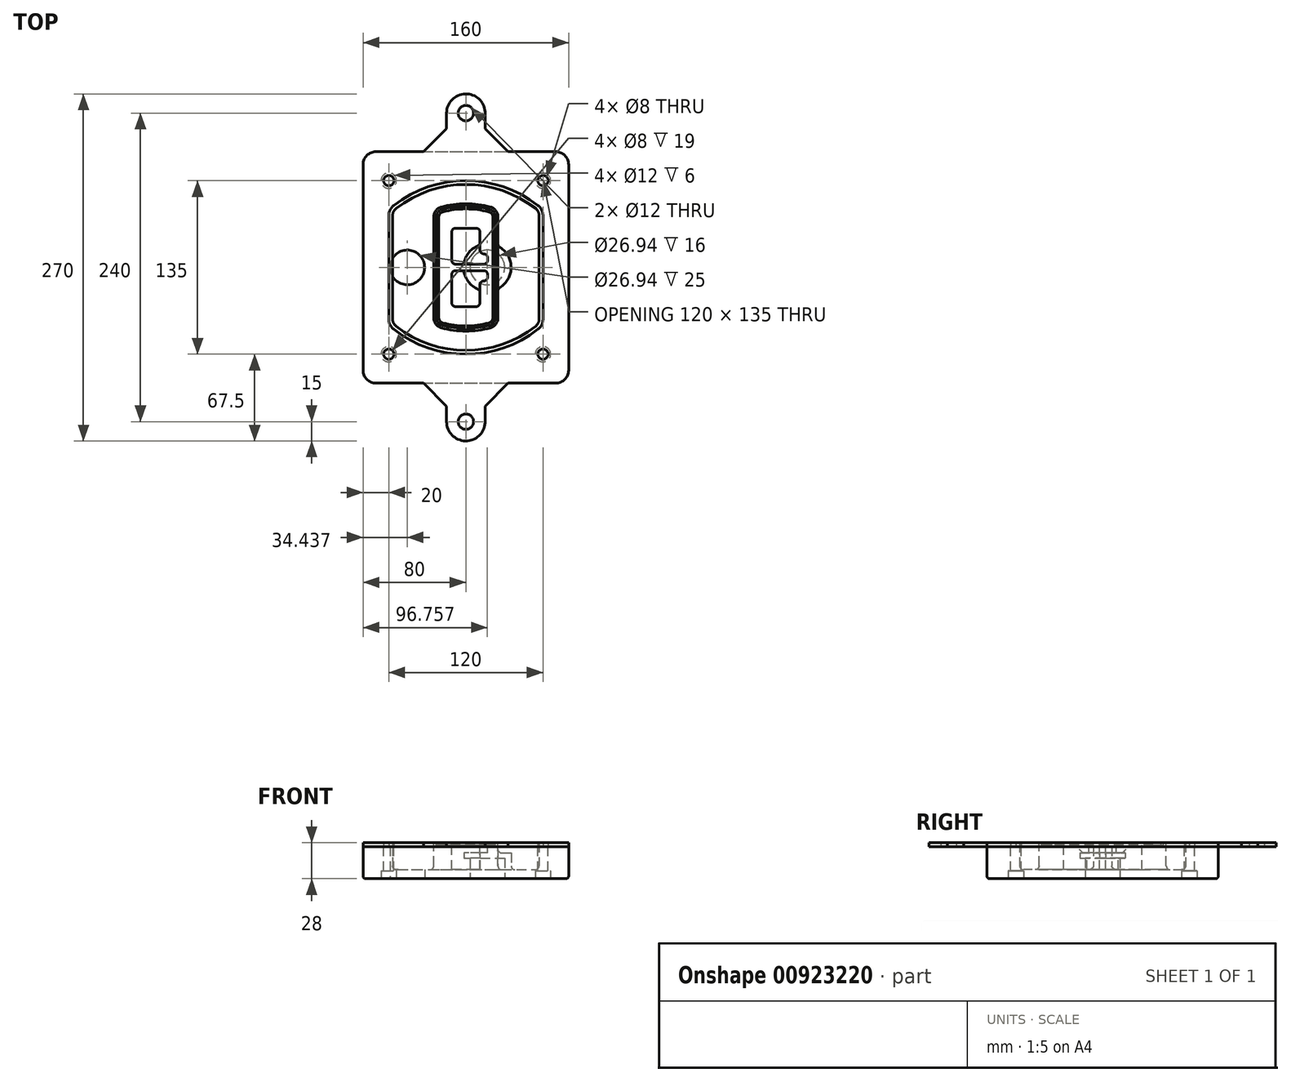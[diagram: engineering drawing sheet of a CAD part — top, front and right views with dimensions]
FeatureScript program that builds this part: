
annotation { "Feature Type Name" : "Feature", "Feature Type Description" : "" }
export const myFeature = defineFeature(function(context is Context, id is Id, definition is map)
    precondition{}
    {
        {
            var Q0;
            Q0=qCreatedBy(makeId("Top.planeOp"),FACE);
            var sketch = newSketch(context, id + "F0", { "sketchPlane" : qUnion([Q0])});
            skPoint(sketch, "E0.rect.middle", {"position": v(0, 0) * mm});
            skLineSegment(sketch, "E1.bottom", {"start": v(-70, -90) * mm, "end": v(70, -90) * mm});
            skLineSegment(sketch, "E1.top", {"start": v(-70, 90) * mm, "end": v(70, 90) * mm});
            skLineSegment(sketch, "E1.left", {"start": v(-80, -80) * mm, "end": v(-80, 80) * mm});
            skLineSegment(sketch, "E1.right", {"start": v(80, -80) * mm, "end": v(80, 80) * mm});
            skLineSegment(sketch, "E2", {"start": v(-80, 90) * mm, "end": v(80, -90) * mm, "construction": true});
            skLineSegment(sketch, "E3", {"start": v(80, 90) * mm, "end": v(-80, -90) * mm, "construction": true});
            skCircle(sketch, "E4", {"center": v(-60, 67.5) * mm, "radius": 4 * mm});
            skCircle(sketch, "E5", {"center": v(60, 67.5) * mm, "radius": 4 * mm});
            skCircle(sketch, "E6", {"center": v(60, -67.5) * mm, "radius": 4 * mm});
            skCircle(sketch, "E7", {"center": v(-60, -67.5) * mm, "radius": 4 * mm});
            skLineSegment(sketch, "E8", {"start": v(-60, 67.5) * mm, "end": v(60, 67.5) * mm, "construction": true});
            skLineSegment(sketch, "E9", {"start": v(60, 67.5) * mm, "end": v(60, -67.5) * mm, "construction": true});
            skLineSegment(sketch, "E10", {"start": v(60, -67.5) * mm, "end": v(-60, -67.5) * mm, "construction": true});
            skLineSegment(sketch, "E11", {"start": v(-60, -67.5) * mm, "end": v(-60, 67.5) * mm, "construction": true});
            skLineSegment(sketch, "E12", {"start": v(-60, 40.3) * mm, "end": v(-60, -40.3) * mm});
            skLineSegment(sketch, "E13", {"start": v(60, 40.3) * mm, "end": v(60, -40.3) * mm});
            skArc(sketch, "E14", {"start": v(56.15, 48.18) * mm, "mid": v(0, 67.5) * mm, "end": v(-56.15, 48.18) * mm});
            skArc(sketch, "E15", {"start": v(-56.15, -48.18) * mm, "mid": v(0, -67.5) * mm, "end": v(56.15, -48.18) * mm});
            skLineSegment(sketch, "E16", {"start": v(-60, 0) * mm, "end": v(60, 0) * mm, "construction": true});
            skPoint(sketch, "E17.visualSharp", {"position": v(-60, -45) * mm});
            skArc(sketch, "E17.filletArc", {"start": v(-60, -40.3) * mm, "mid": v(-58.99, -44.68) * mm, "end": v(-56.15, -48.18) * mm});
            skPoint(sketch, "E18.visualSharp", {"position": v(-60, 45) * mm});
            skArc(sketch, "E18.filletArc", {"start": v(-56.15, 48.18) * mm, "mid": v(-58.99, 44.68) * mm, "end": v(-60, 40.3) * mm});
            skPoint(sketch, "E19.visualSharp", {"position": v(60, 45) * mm});
            skArc(sketch, "E19.filletArc", {"start": v(60, 40.3) * mm, "mid": v(58.99, 44.68) * mm, "end": v(56.15, 48.18) * mm});
            skPoint(sketch, "E20.visualSharp", {"position": v(60, -45) * mm});
            skArc(sketch, "E20.filletArc", {"start": v(56.15, -48.18) * mm, "mid": v(58.99, -44.68) * mm, "end": v(60, -40.3) * mm});
            skPoint(sketch, "E21.visualSharp", {"position": v(-80, 90) * mm});
            skArc(sketch, "E21.filletArc", {"start": v(-70, 90) * mm, "mid": v(-77.07, 87.07) * mm, "end": v(-80, 80) * mm});
            skPoint(sketch, "E22.visualSharp", {"position": v(80, 90) * mm});
            skArc(sketch, "E22.filletArc", {"start": v(80, 80) * mm, "mid": v(77.07, 87.07) * mm, "end": v(70, 90) * mm});
            skPoint(sketch, "E23.visualSharp", {"position": v(80, -90) * mm});
            skArc(sketch, "E23.filletArc", {"start": v(70, -90) * mm, "mid": v(77.07, -87.07) * mm, "end": v(80, -80) * mm});
            skPoint(sketch, "E24.visualSharp", {"position": v(-80, -90) * mm});
            skArc(sketch, "E24.filletArc", {"start": v(-80, -80) * mm, "mid": v(-77.07, -87.07) * mm, "end": v(-70, -90) * mm});
            skArc(sketch, "E25.0", {"start": v(57, 40.3) * mm, "mid": v(56.3, 43.36) * mm, "end": v(54.3, 45.81) * mm});
            skLineSegment(sketch, "E25.1", {"start": v(57, 40.3) * mm, "end": v(57, -40.3) * mm});
            skArc(sketch, "E25.2", {"start": v(54.3, -45.81) * mm, "mid": v(56.3, -43.36) * mm, "end": v(57, -40.3) * mm});
            skArc(sketch, "E25.3", {"start": v(-54.3, -45.81) * mm, "mid": v(0, -64.5) * mm, "end": v(54.3, -45.81) * mm});
            skArc(sketch, "E25.4", {"start": v(-57, -40.3) * mm, "mid": v(-56.3, -43.36) * mm, "end": v(-54.3, -45.81) * mm});
            skArc(sketch, "E25.5", {"start": v(54.3, 45.81) * mm, "mid": v(0, 64.5) * mm, "end": v(-54.3, 45.81) * mm});
            skLineSegment(sketch, "E25.6", {"start": v(-57, 40.3) * mm, "end": v(-57, -40.3) * mm});
            skArc(sketch, "E25.7", {"start": v(-54.3, 45.81) * mm, "mid": v(-56.3, 43.36) * mm, "end": v(-57, 40.3) * mm});
            skArc(sketch, "E26.0", {"start": v(-58.62, 51.33) * mm, "mid": v(-62.58, 46.43) * mm, "end": v(-64, 40.3) * mm});
            skArc(sketch, "E26.1", {"start": v(58.62, 51.33) * mm, "mid": v(0, 71.5) * mm, "end": v(-58.62, 51.33) * mm});
            skArc(sketch, "E26.2", {"start": v(64, 40.3) * mm, "mid": v(62.58, 46.43) * mm, "end": v(58.62, 51.33) * mm});
            skLineSegment(sketch, "E26.3", {"start": v(64, 40.3) * mm, "end": v(64, -40.3) * mm});
            skArc(sketch, "E26.4", {"start": v(58.62, -51.33) * mm, "mid": v(62.58, -46.43) * mm, "end": v(64, -40.3) * mm});
            skLineSegment(sketch, "E26.5", {"start": v(-64, 40.3) * mm, "end": v(-64, -40.3) * mm});
            skArc(sketch, "E26.6", {"start": v(-58.62, -51.33) * mm, "mid": v(0, -71.5) * mm, "end": v(58.62, -51.33) * mm});
            skArc(sketch, "E26.7", {"start": v(-64, -40.3) * mm, "mid": v(-62.58, -46.43) * mm, "end": v(-58.62, -51.33) * mm});
            skSolve(sketch);
        }
        {
            var Q0;
            Q0=makeQuery(id+"F0.imprint","IMPRINT",FACE,{"disambiguationData":[TD([[makeQuery(id+"F0.imprint","IMPRINT",EDGE,{"derivedFrom":sQuery(id+"F0.wireOp",EDGE,"E1.bottom")}),1.0]])]});
            var Q1;
            Q1=makeQuery(id+"F0.imprint","IMPRINT",FACE,{"disambiguationData":[TD([[makeQuery(id+"F0.imprint","IMPRINT",EDGE,{"derivedFrom":sQuery(id+"F0.wireOp",EDGE,"E12")}),1.0]])]});
            var Q2;
            Q2=makeQuery(id+"F0.imprint","IMPRINT",FACE,{"disambiguationData":[TD([[makeQuery(id+"F0.imprint","IMPRINT",EDGE,{"derivedFrom":sQuery(id+"F0.wireOp",EDGE,"E25.0")}),1.0]])]});
            var Q3;
            Q3=makeQuery(id+"F0.imprint","IMPRINT",FACE,{"disambiguationData":[TD([[makeQuery(id+"F0.imprint","IMPRINT",EDGE,{"derivedFrom":sQuery(id+"F0.wireOp",EDGE,"E12")}),-1.0]])]});
            extrude(context, id + "F1", {"entities" : qUnion([Q0, Q1, Q2, Q3]), "oppositeDirection" : true, "depth" : 25 * mm});
        }
        {
            var Q0;
            Q0=makeQuery(id+"F0.imprint","IMPRINT",FACE,{"disambiguationData":[TD([[makeQuery(id+"F0.imprint","IMPRINT",EDGE,{"derivedFrom":sQuery(id+"F0.wireOp",EDGE,"E12")}),1.0]])]});
            extrude(context, id + "F2", {"entities" : qUnion([Q0]), "operationType" : NewBodyOperationType.ADD, "depth" : 3 * mm});
        }
        {
            var Q0;
            Q0=makeQuery(id+"F0.imprint","IMPRINT",FACE,{"disambiguationData":[TD([[makeQuery(id+"F0.imprint","IMPRINT",EDGE,{"derivedFrom":sQuery(id+"F0.wireOp",EDGE,"E25.0")}),1.0]])]});
            extrude(context, id + "F3", {"entities" : qUnion([Q0]), "operationType" : NewBodyOperationType.REMOVE, "oppositeDirection" : true, "depth" : 18 * mm});
        }
        {
            var Q0;
            Q0=makeQuery(id+"F2.opExtrude","CAP_FACE",FACE,{"disambiguationData":[OSD([sQuery(id+"F0.wireOp",EDGE,"E12"),sQuery(id+"F0.wireOp",EDGE,"E13"),sQuery(id+"F0.wireOp",EDGE,"E14"),sQuery(id+"F0.wireOp",EDGE,"E15"),sQuery(id+"F0.wireOp",EDGE,"E17.filletArc"),sQuery(id+"F0.wireOp",EDGE,"E18.filletArc"),sQuery(id+"F0.wireOp",EDGE,"E19.filletArc"),sQuery(id+"F0.wireOp",EDGE,"E20.filletArc"),sQuery(id+"F0.wireOp",EDGE,"E25.0"),sQuery(id+"F0.wireOp",EDGE,"E25.1"),sQuery(id+"F0.wireOp",EDGE,"E25.2"),sQuery(id+"F0.wireOp",EDGE,"E25.3"),sQuery(id+"F0.wireOp",EDGE,"E25.4"),sQuery(id+"F0.wireOp",EDGE,"E25.5"),sQuery(id+"F0.wireOp",EDGE,"E25.6"),sQuery(id+"F0.wireOp",EDGE,"E25.7")])],"isStart":false});
            var sketch = newSketch(context, id + "F4", { "sketchPlane" : qUnion([Q0])});
            skArc(sketch, "E27.0", {"start": v(-19.08, -46.97) * mm, "mid": v(0, -49.5) * mm, "end": v(19.08, -46.97) * mm});
            skArc(sketch, "E28.0", {"start": v(19.08, 46.97) * mm, "mid": v(0, 49.5) * mm, "end": v(-19.08, 46.97) * mm});
            skLineSegment(sketch, "E29", {"start": v(-25, 39.25) * mm, "end": v(-25, -39.25) * mm});
            skLineSegment(sketch, "E30", {"start": v(25, 39.25) * mm, "end": v(25, -39.25) * mm});
            skLineSegment(sketch, "E31", {"start": v(-25, 45.1) * mm, "end": v(25, 45.1) * mm, "construction": true});
            skLineSegment(sketch, "E32", {"start": v(-25, -45.1) * mm, "end": v(25, -45.1) * mm, "construction": true});
            skPoint(sketch, "E33.visualSharp", {"position": v(-25, 45.1) * mm});
            skArc(sketch, "E33.filletArc", {"start": v(-19.08, 46.97) * mm, "mid": v(-23.35, 44.11) * mm, "end": v(-25, 39.25) * mm});
            skPoint(sketch, "E34.visualSharp", {"position": v(25, 45.1) * mm});
            skArc(sketch, "E34.filletArc", {"start": v(25, 39.25) * mm, "mid": v(23.35, 44.11) * mm, "end": v(19.08, 46.97) * mm});
            skPoint(sketch, "E35.visualSharp", {"position": v(25, -45.1) * mm});
            skArc(sketch, "E35.filletArc", {"start": v(19.08, -46.97) * mm, "mid": v(23.35, -44.11) * mm, "end": v(25, -39.25) * mm});
            skPoint(sketch, "E36.visualSharp", {"position": v(-25, -45.1) * mm});
            skArc(sketch, "E36.filletArc", {"start": v(-25, -39.25) * mm, "mid": v(-23.35, -44.11) * mm, "end": v(-19.08, -46.97) * mm});
            skArc(sketch, "E37.0", {"start": v(54.3, 45.81) * mm, "mid": v(0, 64.5) * mm, "end": v(-54.3, 45.81) * mm});
            skArc(sketch, "E37.1", {"start": v(-54.3, 45.81) * mm, "mid": v(-56.3, 43.36) * mm, "end": v(-57, 40.3) * mm});
            skLineSegment(sketch, "E37.2", {"start": v(-57, 40.3) * mm, "end": v(-57, -40.3) * mm});
            skArc(sketch, "E37.3", {"start": v(-57, -40.3) * mm, "mid": v(-56.3, -43.36) * mm, "end": v(-54.3, -45.81) * mm});
            skArc(sketch, "E37.4", {"start": v(-54.3, -45.81) * mm, "mid": v(0, -64.5) * mm, "end": v(54.3, -45.81) * mm});
            skArc(sketch, "E37.5", {"start": v(54.3, -45.81) * mm, "mid": v(56.3, -43.36) * mm, "end": v(57, -40.3) * mm});
            skLineSegment(sketch, "E37.6", {"start": v(57, 40.3) * mm, "end": v(57, -40.3) * mm});
            skArc(sketch, "E37.7", {"start": v(57, 40.3) * mm, "mid": v(56.3, 43.36) * mm, "end": v(54.3, 45.81) * mm});
            skLineSegment(sketch, "E38.0", {"start": v(23, 39.25) * mm, "end": v(23, -39.25) * mm});
            skArc(sketch, "E38.1", {"start": v(18.56, -45.04) * mm, "mid": v(21.76, -42.9) * mm, "end": v(23, -39.25) * mm});
            skArc(sketch, "E38.2", {"start": v(-18.56, -45.04) * mm, "mid": v(0, -47.5) * mm, "end": v(18.56, -45.04) * mm});
            skArc(sketch, "E38.3", {"start": v(-23, -39.25) * mm, "mid": v(-21.76, -42.9) * mm, "end": v(-18.56, -45.04) * mm});
            skLineSegment(sketch, "E38.4", {"start": v(-23, 39.25) * mm, "end": v(-23, -39.25) * mm});
            skArc(sketch, "E38.5", {"start": v(23, 39.25) * mm, "mid": v(21.76, 42.9) * mm, "end": v(18.56, 45.04) * mm});
            skArc(sketch, "E38.6", {"start": v(-18.56, 45.04) * mm, "mid": v(-21.76, 42.9) * mm, "end": v(-23, 39.25) * mm});
            skArc(sketch, "E38.7", {"start": v(18.56, 45.04) * mm, "mid": v(0, 47.5) * mm, "end": v(-18.56, 45.04) * mm});
            skArc(sketch, "E39.0", {"start": v(21, 39.25) * mm, "mid": v(20.18, 41.68) * mm, "end": v(18.04, 43.1) * mm});
            skLineSegment(sketch, "E39.1", {"start": v(21, 39.25) * mm, "end": v(21, -39.25) * mm});
            skArc(sketch, "E39.2", {"start": v(18.04, -43.1) * mm, "mid": v(20.18, -41.68) * mm, "end": v(21, -39.25) * mm});
            skArc(sketch, "E39.3", {"start": v(-18.04, -43.1) * mm, "mid": v(0, -45.5) * mm, "end": v(18.04, -43.1) * mm});
            skArc(sketch, "E39.4", {"start": v(-21, -39.25) * mm, "mid": v(-20.18, -41.68) * mm, "end": v(-18.04, -43.1) * mm});
            skArc(sketch, "E39.5", {"start": v(18.04, 43.1) * mm, "mid": v(0, 45.5) * mm, "end": v(-18.04, 43.1) * mm});
            skLineSegment(sketch, "E39.6", {"start": v(-21, 39.25) * mm, "end": v(-21, -39.25) * mm});
            skArc(sketch, "E39.7", {"start": v(-18.04, 43.1) * mm, "mid": v(-20.18, 41.68) * mm, "end": v(-21, 39.25) * mm});
            skLineSegment(sketch, "E40", {"start": v(-25, 0) * mm, "end": v(25, 0) * mm, "construction": true});
            skLineSegment(sketch, "E41", {"start": v(-11, 5.5) * mm, "end": v(-11, 27.5) * mm});
            skLineSegment(sketch, "E42", {"start": v(-8, 30.5) * mm, "end": v(8, 30.5) * mm});
            skLineSegment(sketch, "E43", {"start": v(11, 27.5) * mm, "end": v(11, 13.5) * mm});
            skLineSegment(sketch, "E44", {"start": v(14, 10.5) * mm, "end": v(14, 10.5) * mm});
            skLineSegment(sketch, "E45", {"start": v(17, 7.5) * mm, "end": v(17, 5.5) * mm});
            skLineSegment(sketch, "E46", {"start": v(14, 2.5) * mm, "end": v(-8, 2.5) * mm});
            skPoint(sketch, "E47.visualSharp", {"position": v(-11, 30.5) * mm});
            skArc(sketch, "E47.filletArc", {"start": v(-8, 30.5) * mm, "mid": v(-10.12, 29.62) * mm, "end": v(-11, 27.5) * mm});
            skPoint(sketch, "E48.visualSharp", {"position": v(11, 30.5) * mm});
            skArc(sketch, "E48.filletArc", {"start": v(11, 27.5) * mm, "mid": v(10.12, 29.62) * mm, "end": v(8, 30.5) * mm});
            skPoint(sketch, "E49.visualSharp", {"position": v(11, 10.5) * mm});
            skArc(sketch, "E49.filletArc", {"start": v(11, 13.5) * mm, "mid": v(11.88, 11.38) * mm, "end": v(14, 10.5) * mm});
            skPoint(sketch, "E50.visualSharp", {"position": v(17, 10.5) * mm});
            skArc(sketch, "E50.filletArc", {"start": v(17, 7.5) * mm, "mid": v(16.12, 9.62) * mm, "end": v(14, 10.5) * mm});
            skPoint(sketch, "E51.visualSharp", {"position": v(17, 2.5) * mm});
            skArc(sketch, "E51.filletArc", {"start": v(14, 2.5) * mm, "mid": v(16.12, 3.38) * mm, "end": v(17, 5.5) * mm});
            skPoint(sketch, "E52.visualSharp", {"position": v(-11, 2.5) * mm});
            skArc(sketch, "E52.filletArc", {"start": v(-11, 5.5) * mm, "mid": v(-10.12, 3.38) * mm, "end": v(-8, 2.5) * mm});
            skLineSegment(sketch, "E53.0.MirrorCS", {"start": v(14, -2.5) * mm, "end": v(-8, -2.5) * mm});
            skArc(sketch, "E54.0.MirrorCS", {"start": v(-11, -5.5) * mm, "mid": v(-10.12, -3.38) * mm, "end": v(-8, -2.5) * mm});
            skLineSegment(sketch, "E55.0.MirrorCS", {"start": v(-11, -5.5) * mm, "end": v(-11, -27.5) * mm});
            skArc(sketch, "E56.0.MirrorCS", {"start": v(-8, -30.5) * mm, "mid": v(-10.12, -29.62) * mm, "end": v(-11, -27.5) * mm});
            skLineSegment(sketch, "E57.0.MirrorCS", {"start": v(-8, -30.5) * mm, "end": v(8, -30.5) * mm});
            skArc(sketch, "E58.0.MirrorCS", {"start": v(11, -27.5) * mm, "mid": v(10.12, -29.62) * mm, "end": v(8, -30.5) * mm});
            skLineSegment(sketch, "E59.0.MirrorCS", {"start": v(11, -27.5) * mm, "end": v(11, -13.5) * mm});
            skArc(sketch, "E60.0.MirrorCS", {"start": v(11, -13.5) * mm, "mid": v(11.88, -11.38) * mm, "end": v(14, -10.5) * mm});
            skArc(sketch, "E61.0.MirrorCS", {"start": v(17, -7.5) * mm, "mid": v(16.12, -9.62) * mm, "end": v(14, -10.5) * mm});
            skLineSegment(sketch, "E62.0.MirrorCS", {"start": v(17, -7.5) * mm, "end": v(17, -5.5) * mm});
            skArc(sketch, "E63.0.MirrorCS", {"start": v(14, -2.5) * mm, "mid": v(16.12, -3.38) * mm, "end": v(17, -5.5) * mm});
            skSolve(sketch);
        }
        {
            var Q0;
            Q0=makeQuery(id+"F4.imprint","IMPRINT",FACE,{"disambiguationData":[TD([[makeQuery(id+"F4.imprint","IMPRINT",EDGE,{"derivedFrom":sQuery(id+"F4.wireOp",EDGE,"E27.0")}),1.0]])]});
            var Q1;
            Q1=makeQuery(id+"F4.imprint","IMPRINT",FACE,{"disambiguationData":[TD([[makeQuery(id+"F4.imprint","IMPRINT",EDGE,{"derivedFrom":sQuery(id+"F4.wireOp",EDGE,"E38.0")}),-1.0]])]});
            var Q2;
            Q2=makeQuery(id+"F4.imprint","IMPRINT",FACE,{"disambiguationData":[TD([[makeQuery(id+"F4.imprint","IMPRINT",EDGE,{"derivedFrom":sQuery(id+"F4.wireOp",EDGE,"E39.0")}),1.0]])]});
            extrude(context, id + "F5", {"entities" : qUnion([Q0, Q1, Q2]), "operationType" : NewBodyOperationType.ADD, "endBound" : BoundingType.UP_TO_NEXT, "oppositeDirection" : true, "depth" : 25 * mm});
        }
        {
            var Q0;
            Q0=makeQuery(id+"F4.imprint","IMPRINT",FACE,{"disambiguationData":[TD([[makeQuery(id+"F4.imprint","IMPRINT",EDGE,{"derivedFrom":sQuery(id+"F4.wireOp",EDGE,"E38.0")}),-1.0]])]});
            extrude(context, id + "F6", {"entities" : qUnion([Q0]), "operationType" : NewBodyOperationType.REMOVE, "oppositeDirection" : true, "depth" : 2 * mm});
        }
        {
            var Q0;
            Q0=makeQuery(id+"F1.opExtrude","CAP_FACE",FACE,{"disambiguationData":[OSD([sQuery(id+"F0.wireOp",EDGE,"E1.bottom"),sQuery(id+"F0.wireOp",EDGE,"E1.top"),sQuery(id+"F0.wireOp",EDGE,"E1.left"),sQuery(id+"F0.wireOp",EDGE,"E1.right"),sQuery(id+"F0.wireOp",EDGE,"E4"),sQuery(id+"F0.wireOp",EDGE,"E5"),sQuery(id+"F0.wireOp",EDGE,"E6"),sQuery(id+"F0.wireOp",EDGE,"E7"),sQuery(id+"F0.wireOp",EDGE,"E21.filletArc"),sQuery(id+"F0.wireOp",EDGE,"E22.filletArc"),sQuery(id+"F0.wireOp",EDGE,"E23.filletArc"),sQuery(id+"F0.wireOp",EDGE,"E24.filletArc")])],"isStart":false});
            var sketch = newSketch(context, id + "F7", { "sketchPlane" : qUnion([Q0])});
            skCircle(sketch, "E64", {"center": v(16.76, 0) * mm, "radius": 13.47 * mm});
            skCircle(sketch, "E65", {"center": v(-45.56, 0) * mm, "radius": 13.47 * mm});
            skLineSegment(sketch, "E66", {"start": v(80, 0) * mm, "end": v(-80, 0) * mm});
            skCircle(sketch, "E67", {"center": v(16.76, 0) * mm, "radius": 18.47 * mm});
            skCircle(sketch, "E68", {"center": v(60, -67.5) * mm, "radius": 6 * mm});
            skCircle(sketch, "E69", {"center": v(-60, -67.5) * mm, "radius": 6 * mm});
            skCircle(sketch, "E70", {"center": v(-60, 67.5) * mm, "radius": 6 * mm});
            skCircle(sketch, "E71", {"center": v(60, 67.5) * mm, "radius": 6 * mm});
            skSolve(sketch);
        }
        {
            var Q0;
            {var subQ1=sQuery(id+"F7.wireOp",EDGE,"E66");var subQ4=sQuery(id+"F7.wireOp",EDGE,"E64");var subQ6=makeQuery(id+"F7.imprint","INTERSECT",VERTEX,{"disambiguationData":[OD(0.0)],"derivedFrom":[subQ4,subQ1]});Q0=makeQuery(id+"F7.imprint","IMPRINT",FACE,{"disambiguationData":[TD([[makeQuery(id+"F7.imprint","IMPRINT",EDGE,{"disambiguationData":[TD([[subQ6,-1.0]])],"derivedFrom":subQ4}),-1.0]])]});}
            var Q1;
            {var subQ0=sQuery(id+"F7.wireOp",EDGE,"E66");var subQ1=sQuery(id+"F7.wireOp",EDGE,"E64");var subQ3=makeQuery(id+"F7.imprint","INTERSECT",VERTEX,{"disambiguationData":[OD(0.0)],"derivedFrom":[subQ1,subQ0]});Q1=makeQuery(id+"F7.imprint","IMPRINT",FACE,{"disambiguationData":[TD([[makeQuery(id+"F7.imprint","IMPRINT",EDGE,{"disambiguationData":[TD([[subQ3,-1.0]])],"derivedFrom":subQ1}),1.0]])]});}
            var Q2;
            {var subQ0=sQuery(id+"F7.wireOp",EDGE,"E66");var subQ1=sQuery(id+"F7.wireOp",EDGE,"E64");var subQ3=makeQuery(id+"F7.imprint","INTERSECT",VERTEX,{"disambiguationData":[OD(0.0)],"derivedFrom":[subQ1,subQ0]});Q2=makeQuery(id+"F7.imprint","IMPRINT",FACE,{"disambiguationData":[TD([[makeQuery(id+"F7.imprint","IMPRINT",EDGE,{"disambiguationData":[TD([[subQ3,1.0]])],"derivedFrom":subQ1}),1.0]])]});}
            var Q3;
            {var subQ1=sQuery(id+"F7.wireOp",EDGE,"E66");var subQ4=sQuery(id+"F7.wireOp",EDGE,"E64");var subQ6=makeQuery(id+"F7.imprint","INTERSECT",VERTEX,{"disambiguationData":[OD(0.0)],"derivedFrom":[subQ4,subQ1]});Q3=makeQuery(id+"F7.imprint","IMPRINT",FACE,{"disambiguationData":[TD([[makeQuery(id+"F7.imprint","IMPRINT",EDGE,{"disambiguationData":[TD([[subQ6,1.0]])],"derivedFrom":subQ4}),-1.0]])]});}
            extrude(context, id + "F8", {"entities" : qUnion([Q0, Q1, Q2, Q3]), "operationType" : NewBodyOperationType.ADD, "oppositeDirection" : true, "depth" : 20 * mm});
        }
        {
            var Q0;
            {var subQ0=sQuery(id+"F7.wireOp",EDGE,"E66");var subQ1=sQuery(id+"F7.wireOp",EDGE,"E64");var subQ3=makeQuery(id+"F7.imprint","INTERSECT",VERTEX,{"disambiguationData":[OD(0.0)],"derivedFrom":[subQ1,subQ0]});Q0=makeQuery(id+"F7.imprint","IMPRINT",FACE,{"disambiguationData":[TD([[makeQuery(id+"F7.imprint","IMPRINT",EDGE,{"disambiguationData":[TD([[subQ3,-1.0]])],"derivedFrom":subQ1}),1.0]])]});}
            var Q1;
            {var subQ0=sQuery(id+"F7.wireOp",EDGE,"E66");var subQ1=sQuery(id+"F7.wireOp",EDGE,"E64");var subQ3=makeQuery(id+"F7.imprint","INTERSECT",VERTEX,{"disambiguationData":[OD(0.0)],"derivedFrom":[subQ1,subQ0]});Q1=makeQuery(id+"F7.imprint","IMPRINT",FACE,{"disambiguationData":[TD([[makeQuery(id+"F7.imprint","IMPRINT",EDGE,{"disambiguationData":[TD([[subQ3,1.0]])],"derivedFrom":subQ1}),1.0]])]});}
            extrude(context, id + "F9", {"entities" : qUnion([Q0, Q1]), "operationType" : NewBodyOperationType.REMOVE, "oppositeDirection" : true, "depth" : 16 * mm});
        }
        {
            var Q0;
            {var subQ0=sQuery(id+"F7.wireOp",EDGE,"E66");var subQ1=sQuery(id+"F7.wireOp",EDGE,"E65");var subQ3=makeQuery(id+"F7.imprint","INTERSECT",VERTEX,{"disambiguationData":[OD(0.0)],"derivedFrom":[subQ1,subQ0]});Q0=makeQuery(id+"F7.imprint","IMPRINT",FACE,{"disambiguationData":[TD([[makeQuery(id+"F7.imprint","IMPRINT",EDGE,{"disambiguationData":[TD([[subQ3,-1.0]])],"derivedFrom":subQ1}),1.0]])]});}
            var Q1;
            {var subQ0=sQuery(id+"F7.wireOp",EDGE,"E66");var subQ1=sQuery(id+"F7.wireOp",EDGE,"E65");var subQ3=makeQuery(id+"F7.imprint","INTERSECT",VERTEX,{"disambiguationData":[OD(0.0)],"derivedFrom":[subQ1,subQ0]});Q1=makeQuery(id+"F7.imprint","IMPRINT",FACE,{"disambiguationData":[TD([[makeQuery(id+"F7.imprint","IMPRINT",EDGE,{"disambiguationData":[TD([[subQ3,1.0]])],"derivedFrom":subQ1}),1.0]])]});}
            extrude(context, id + "F10", {"entities" : qUnion([Q0, Q1]), "operationType" : NewBodyOperationType.REMOVE, "oppositeDirection" : true, "depth" : 25 * mm});
        }
        {
            var Q0;
            Q0=makeQuery(id+"F7.imprint","IMPRINT",FACE,{"disambiguationData":[TD([[makeQuery(id+"F7.imprint","IMPRINT",EDGE,{"derivedFrom":sQuery(id+"F7.wireOp",EDGE,"E68")}),1.0]])]});
            var Q1;
            Q1=makeQuery(id+"F7.imprint","IMPRINT",FACE,{"disambiguationData":[TD([[makeQuery(id+"F7.imprint","IMPRINT",EDGE,{"derivedFrom":makeQuery(id+"F1.opExtrude","CAP_EDGE",EDGE,{"disambiguationData":[OSD([sQuery(id+"F0.wireOp",EDGE,"E5")])],"isStart":false})}),-1.0]])]});
            var Q2;
            Q2=makeQuery(id+"F7.imprint","IMPRINT",FACE,{"disambiguationData":[TD([[makeQuery(id+"F7.imprint","IMPRINT",EDGE,{"derivedFrom":sQuery(id+"F7.wireOp",EDGE,"E69")}),1.0]])]});
            var Q3;
            Q3=makeQuery(id+"F7.imprint","IMPRINT",FACE,{"disambiguationData":[TD([[makeQuery(id+"F7.imprint","IMPRINT",EDGE,{"derivedFrom":makeQuery(id+"F1.opExtrude","CAP_EDGE",EDGE,{"disambiguationData":[OSD([sQuery(id+"F0.wireOp",EDGE,"E4")])],"isStart":false})}),-1.0]])]});
            var Q4;
            Q4=makeQuery(id+"F7.imprint","IMPRINT",FACE,{"disambiguationData":[TD([[makeQuery(id+"F7.imprint","IMPRINT",EDGE,{"derivedFrom":sQuery(id+"F7.wireOp",EDGE,"E70")}),1.0]])]});
            var Q5;
            Q5=makeQuery(id+"F7.imprint","IMPRINT",FACE,{"disambiguationData":[TD([[makeQuery(id+"F7.imprint","IMPRINT",EDGE,{"derivedFrom":makeQuery(id+"F1.opExtrude","CAP_EDGE",EDGE,{"disambiguationData":[OSD([sQuery(id+"F0.wireOp",EDGE,"E7")])],"isStart":false})}),-1.0]])]});
            var Q6;
            Q6=makeQuery(id+"F7.imprint","IMPRINT",FACE,{"disambiguationData":[TD([[makeQuery(id+"F7.imprint","IMPRINT",EDGE,{"derivedFrom":sQuery(id+"F7.wireOp",EDGE,"E71")}),1.0]])]});
            var Q7;
            Q7=makeQuery(id+"F7.imprint","IMPRINT",FACE,{"disambiguationData":[TD([[makeQuery(id+"F7.imprint","IMPRINT",EDGE,{"derivedFrom":makeQuery(id+"F1.opExtrude","CAP_EDGE",EDGE,{"disambiguationData":[OSD([sQuery(id+"F0.wireOp",EDGE,"E6")])],"isStart":false})}),-1.0]])]});
            extrude(context, id + "F11", {"entities" : qUnion([Q0, Q1, Q2, Q3, Q4, Q5, Q6, Q7]), "operationType" : NewBodyOperationType.REMOVE, "oppositeDirection" : true, "depth" : 6 * mm});
        }
        {
            var Q0;
            Q0=makeQuery(id+"F9.boolean.opBoolean","COPY",FACE,{"derivedFrom":makeQuery(id+"F9.opExtrude","CAP_FACE",FACE,{"disambiguationData":[OSD([sQuery(id+"F7.wireOp",EDGE,"E64")])],"isStart":false})});
            var sketch = newSketch(context, id + "F12", { "sketchPlane" : qUnion([Q0])});
            skArc(sketch, "E72.0", {"start": v(11, 17.55) * mm, "mid": v(2.57, 11.82) * mm, "end": v(-1.54, 2.5) * mm});
            skArc(sketch, "E72.1", {"start": v(-1.54, -2.5) * mm, "mid": v(2.57, -11.82) * mm, "end": v(11, -17.55) * mm});
            skLineSegment(sketch, "E73", {"start": v(-1.54, -2.5) * mm, "end": v(14, -2.5) * mm});
            skLineSegment(sketch, "E74.0", {"start": v(14, 2.5) * mm, "end": v(-1.54, 2.5) * mm});
            skArc(sketch, "E74.1", {"start": v(14, 2.5) * mm, "mid": v(16.12, 3.38) * mm, "end": v(17, 5.5) * mm});
            skLineSegment(sketch, "E74.2", {"start": v(17, 7.5) * mm, "end": v(17, 5.5) * mm});
            skArc(sketch, "E74.3", {"start": v(17, 7.5) * mm, "mid": v(16.12, 9.62) * mm, "end": v(14, 10.5) * mm});
            skArc(sketch, "E74.4", {"start": v(11, 13.5) * mm, "mid": v(11.88, 11.38) * mm, "end": v(14, 10.5) * mm});
            skLineSegment(sketch, "E74.5", {"start": v(11, 17.55) * mm, "end": v(11, 13.5) * mm});
            skLineSegment(sketch, "E74.7", {"start": v(14, -2.5) * mm, "end": v(-1.54, -2.5) * mm});
            skArc(sketch, "E74.8", {"start": v(14, -2.5) * mm, "mid": v(16.12, -3.38) * mm, "end": v(17, -5.5) * mm});
            skLineSegment(sketch, "E74.9", {"start": v(17, -7.5) * mm, "end": v(17, -5.5) * mm});
            skArc(sketch, "E74.10", {"start": v(17, -7.5) * mm, "mid": v(16.12, -9.62) * mm, "end": v(14, -10.5) * mm});
            skArc(sketch, "E74.11", {"start": v(11, -13.5) * mm, "mid": v(11.88, -11.38) * mm, "end": v(14, -10.5) * mm});
            skLineSegment(sketch, "E74.12", {"start": v(11, -17.55) * mm, "end": v(11, -13.5) * mm});
            skPoint(sketch, "E75.orphan", {"position": v(11, -27.5) * mm});
            skPoint(sketch, "E76.orphan", {"position": v(-8, -2.5) * mm});
            skPoint(sketch, "E77.orphan", {"position": v(-8, 2.5) * mm});
            skPoint(sketch, "E78.orphan", {"position": v(11, 27.5) * mm});
            skSolve(sketch);
        }
        {
            var Q0;
            {var subQ7=sQuery(id+"F12.wireOp",EDGE,"E72.0");var subQ14=sQuery(id+"F12.wireOp",EDGE,"E72.1");var subQ16=sQuery(id+"F12.wireOp",EDGE,"E74.1");var subQ18=sQuery(id+"F12.wireOp",EDGE,"E74.8");Q0=qUnion([makeQuery(id+"F12.imprint","IMPRINT",FACE,{"disambiguationData":[TD([[makeQuery(id+"F12.imprint","IMPRINT",EDGE,{"derivedFrom":subQ7}),1.0]])]}),makeQuery(id+"F12.imprint","IMPRINT",FACE,{"disambiguationData":[TD([[makeQuery(id+"F12.imprint","IMPRINT",EDGE,{"derivedFrom":subQ14}),1.0]])]}),makeQuery(id+"F12.imprint","IMPRINT",FACE,{"disambiguationData":[TD([[makeQuery(id+"F12.imprint","IMPRINT",EDGE,{"derivedFrom":subQ16}),1.0]])]}),makeQuery(id+"F12.imprint","IMPRINT",FACE,{"disambiguationData":[TD([[makeQuery(id+"F12.imprint","IMPRINT",EDGE,{"derivedFrom":subQ18}),-1.0]])]})]);}
            var Q1;
            Q1=makeQuery(id+"F5.boolean.opBoolean","SPLIT",FACE,{"disambiguationData":[TD([makeQuery(id+"F5.opExtrude","SWEPT_FACE",FACE,{"disambiguationData":[OSD([sQuery(id+"F4.wireOp",EDGE,"E41")])]})])],"derivedFrom":makeQuery(id+"F3.boolean.opBoolean","COPY",FACE,{"derivedFrom":makeQuery(id+"F3.opExtrude","CAP_FACE",FACE,{"disambiguationData":[OSD([sQuery(id+"F0.wireOp",EDGE,"E25.0"),sQuery(id+"F0.wireOp",EDGE,"E25.1"),sQuery(id+"F0.wireOp",EDGE,"E25.2"),sQuery(id+"F0.wireOp",EDGE,"E25.3"),sQuery(id+"F0.wireOp",EDGE,"E25.4"),sQuery(id+"F0.wireOp",EDGE,"E25.5"),sQuery(id+"F0.wireOp",EDGE,"E25.6"),sQuery(id+"F0.wireOp",EDGE,"E25.7")])],"isStart":false})})});
            extrude(context, id + "F13", {"entities" : qUnion([Q0]), "operationType" : NewBodyOperationType.REMOVE, "endBound" : BoundingType.UP_TO_SURFACE, "endBoundEntityFace" : qUnion([Q1]), "depth" : 25 * mm});
        }
        {
            var Q0;
            Q0=makeQuery(id+"F3.boolean.opBoolean","COPY",EDGE,{"derivedFrom":makeQuery(id+"F3.opExtrude","CAP_EDGE",EDGE,{"disambiguationData":[OSD([sQuery(id+"F0.wireOp",EDGE,"E25.6")])],"isStart":false})});
            var Q1;
            Q1=makeQuery(id+"F8.boolean.opBoolean","INTERSECT",EDGE,{"derivedFrom":[makeQuery(id+"F5.opExtrude","SWEPT_FACE",FACE,{"disambiguationData":[OSD([sQuery(id+"F4.wireOp",EDGE,"E30")])]}),makeQuery(id+"F8.opExtrude","CAP_FACE",FACE,{"disambiguationData":[OSD([sQuery(id+"F7.wireOp",EDGE,"E67")])],"isStart":false})]});
            var Q2;
            Q2=makeQuery(id+"F8.boolean.opBoolean","INTERSECT",EDGE,{"disambiguationData":[OD(1.0)],"derivedFrom":[makeQuery(id+"F5.opExtrude","SWEPT_FACE",FACE,{"disambiguationData":[OSD([sQuery(id+"F4.wireOp",EDGE,"E30")])]}),makeQuery(id+"F8.opExtrude","SWEPT_FACE",FACE,{"disambiguationData":[OSD([sQuery(id+"F7.wireOp",EDGE,"E67")])]})]});
            var Q3;
            {var subQ0=sQuery(id+"F4.wireOp",EDGE,"E30");Q3=makeQuery(id+"F8.boolean.opBoolean","SPLIT",EDGE,{"disambiguationData":[TD([makeQuery(id+"F5.opExtrude","SWEPT_FACE",FACE,{"disambiguationData":[OSD([sQuery(id+"F4.wireOp",EDGE,"E35.filletArc")])]})])],"derivedFrom":makeQuery(id+"F5.opExtrude","CAP_EDGE",EDGE,{"disambiguationData":[OSD([subQ0])],"isStart":false})});}
            var Q4;
            {var subQ0=sQuery(id+"F0.wireOp",EDGE,"E25.7");var subQ1=sQuery(id+"F0.wireOp",EDGE,"E25.1");var subQ2=sQuery(id+"F0.wireOp",EDGE,"E25.6");var subQ3=sQuery(id+"F0.wireOp",EDGE,"E25.5");var subQ4=sQuery(id+"F0.wireOp",EDGE,"E25.4");var subQ5=sQuery(id+"F0.wireOp",EDGE,"E25.0");var subQ6=sQuery(id+"F0.wireOp",EDGE,"E25.2");var subQ7=sQuery(id+"F0.wireOp",EDGE,"E25.3");Q4=makeQuery(id+"F8.boolean.opBoolean","INTERSECT",EDGE,{"derivedFrom":[makeQuery(id+"F5.boolean.opBoolean","SPLIT",FACE,{"disambiguationData":[TD([makeQuery(id+"F2.opExtrude","SWEPT_FACE",FACE,{"disambiguationData":[OSD([subQ5])]})])],"derivedFrom":makeQuery(id+"F3.boolean.opBoolean","COPY",FACE,{"derivedFrom":makeQuery(id+"F3.opExtrude","CAP_FACE",FACE,{"disambiguationData":[OSD([subQ5,subQ1,subQ6,subQ7,subQ4,subQ3,subQ2,subQ0])],"isStart":false})})}),makeQuery(id+"F8.opExtrude","SWEPT_FACE",FACE,{"disambiguationData":[OSD([sQuery(id+"F7.wireOp",EDGE,"E67")])]})]});}
            var Q5;
            Q5=makeQuery(id+"F8.boolean.opBoolean","INTERSECT",EDGE,{"disambiguationData":[OD(0.0)],"derivedFrom":[makeQuery(id+"F5.opExtrude","SWEPT_FACE",FACE,{"disambiguationData":[OSD([sQuery(id+"F4.wireOp",EDGE,"E30")])]}),makeQuery(id+"F8.opExtrude","SWEPT_FACE",FACE,{"disambiguationData":[OSD([sQuery(id+"F7.wireOp",EDGE,"E67")])]})]});
            fillet(context, id + "F14", {"entities" : qUnion([Q0, Q1, Q2, Q3, Q4, Q5]), "radius" : 3 * mm, "tangentPropagation" : true, "allowEdgeOverflow" : false});
        }
        {
            var Q0;
            Q0=makeQuery(id+"F1.opExtrude","CAP_EDGE",EDGE,{"disambiguationData":[OSD([sQuery(id+"F0.wireOp",EDGE,"E1.bottom")])],"isStart":false});
            fillet(context, id + "F15", {"entities" : qUnion([Q0]), "radius" : 2 * mm, "tangentPropagation" : true, "allowEdgeOverflow" : false});
        }
        {
            var Q0;
            {var subQ0=sQuery(id+"F0.wireOp",EDGE,"E21.filletArc");var subQ1=sQuery(id+"F0.wireOp",EDGE,"E7");var subQ2=sQuery(id+"F0.wireOp",EDGE,"E6");var subQ3=sQuery(id+"F0.wireOp",EDGE,"E5");var subQ4=sQuery(id+"F0.wireOp",EDGE,"E4");var subQ5=sQuery(id+"F0.wireOp",EDGE,"E22.filletArc");var subQ6=sQuery(id+"F0.wireOp",EDGE,"E1.bottom");var subQ7=sQuery(id+"F0.wireOp",EDGE,"E1.right");var subQ8=sQuery(id+"F0.wireOp",EDGE,"E1.top");var subQ9=sQuery(id+"F0.wireOp",EDGE,"E1.left");var subQ10=sQuery(id+"F0.wireOp",EDGE,"E23.filletArc");var subQ11=sQuery(id+"F0.wireOp",EDGE,"E24.filletArc");Q0=makeQuery(id+"F2.boolean.opBoolean","SPLIT",FACE,{"disambiguationData":[TD([makeQuery(id+"F1.opExtrude","SWEPT_FACE",FACE,{"disambiguationData":[OSD([subQ6])]})])],"derivedFrom":makeQuery(id+"F1.opExtrude","CAP_FACE",FACE,{"disambiguationData":[OSD([subQ6,subQ8,subQ9,subQ7,subQ4,subQ3,subQ2,subQ1,subQ0,subQ5,subQ10,subQ11])],"isStart":true})});}
            var sketch = newSketch(context, id + "F16", { "sketchPlane" : qUnion([Q0])});
            skLineSegment(sketch, "E79", {"start": v(-33, 90) * mm, "end": v(-15, 108) * mm});
            skLineSegment(sketch, "E80", {"start": v(-15, 108) * mm, "end": v(-15, 120) * mm});
            skLineSegment(sketch, "E81", {"start": v(32.98, 90) * mm, "end": v(14.98, 108) * mm});
            skLineSegment(sketch, "E82", {"start": v(14.98, 108) * mm, "end": v(14.98, 120.82) * mm});
            skArc(sketch, "E83", {"start": v(14.98, 120.82) * mm, "mid": v(-0.4, 135) * mm, "end": v(-15, 120) * mm});
            skLineSegment(sketch, "E84", {"start": v(0, 90) * mm, "end": v(0, 120) * mm, "construction": true});
            skCircle(sketch, "E85", {"center": v(0, 120) * mm, "radius": 6 * mm});
            skLineSegment(sketch, "E86", {"start": v(32.98, 90) * mm, "end": v(-33, 90) * mm, "construction": true});
            skLineSegment(sketch, "E87", {"start": v(-80, 0) * mm, "end": v(80, 0) * mm, "construction": true});
            skLineSegment(sketch, "E88.MirrorCS", {"start": v(32.98, -90) * mm, "end": v(14.98, -108) * mm});
            skLineSegment(sketch, "E89.MirrorCS", {"start": v(14.98, -108) * mm, "end": v(14.98, -120.82) * mm});
            skArc(sketch, "E90.MirrorCS", {"start": v(14.98, -120.82) * mm, "mid": v(-0.4, -135) * mm, "end": v(-15, -120) * mm});
            skCircle(sketch, "E91.MirrorC", {"center": v(0, -120) * mm, "radius": 6 * mm});
            skLineSegment(sketch, "E92.MirrorCS", {"start": v(-33, -90) * mm, "end": v(-15, -108) * mm});
            skLineSegment(sketch, "E93.MirrorCS", {"start": v(-15, -108) * mm, "end": v(-15, -120) * mm});
            skLineSegment(sketch, "E94.MirrorCS", {"start": v(0, -90) * mm, "end": v(0, -120) * mm, "construction": true});
            skSolve(sketch);
        }
        {
            var Q0;
            {var subQ0=sQuery(id+"F16.wireOp",EDGE,"E88.MirrorCS");Q0=makeQuery(id+"F16.imprint","IMPRINT",FACE,{"disambiguationData":[TD([[makeQuery(id+"F16.imprint","IMPRINT",EDGE,{"derivedFrom":subQ0}),-1.0]])]});}
            var Q1;
            Q1=makeQuery(id+"F16.imprint","IMPRINT",FACE,{"disambiguationData":[TD([[makeQuery(id+"F16.imprint","IMPRINT",EDGE,{"derivedFrom":makeQuery(id+"F1.opExtrude","CAP_EDGE",EDGE,{"disambiguationData":[OSD([sQuery(id+"F0.wireOp",EDGE,"E1.left")])],"isStart":true})}),-1.0]])]});
            var Q2;
            {var subQ1=sQuery(id+"F16.wireOp",EDGE,"E79");Q2=makeQuery(id+"F16.imprint","IMPRINT",FACE,{"disambiguationData":[TD([[makeQuery(id+"F16.imprint","IMPRINT",EDGE,{"derivedFrom":subQ1}),-1.0]])]});}
            var Q3;
            Q3=makeQuery(id+"F2.opExtrude","CAP_FACE",FACE,{"disambiguationData":[OSD([sQuery(id+"F0.wireOp",EDGE,"E12"),sQuery(id+"F0.wireOp",EDGE,"E13"),sQuery(id+"F0.wireOp",EDGE,"E14"),sQuery(id+"F0.wireOp",EDGE,"E15"),sQuery(id+"F0.wireOp",EDGE,"E17.filletArc"),sQuery(id+"F0.wireOp",EDGE,"E18.filletArc"),sQuery(id+"F0.wireOp",EDGE,"E19.filletArc"),sQuery(id+"F0.wireOp",EDGE,"E20.filletArc"),sQuery(id+"F0.wireOp",EDGE,"E25.0"),sQuery(id+"F0.wireOp",EDGE,"E25.1"),sQuery(id+"F0.wireOp",EDGE,"E25.2"),sQuery(id+"F0.wireOp",EDGE,"E25.3"),sQuery(id+"F0.wireOp",EDGE,"E25.4"),sQuery(id+"F0.wireOp",EDGE,"E25.5"),sQuery(id+"F0.wireOp",EDGE,"E25.6"),sQuery(id+"F0.wireOp",EDGE,"E25.7")])],"isStart":false});
            extrude(context, id + "F17", {"entities" : qUnion([Q0, Q1, Q2]), "endBound" : BoundingType.UP_TO_SURFACE, "depth" : 25 * mm, "endBoundEntityFace" : qUnion([Q3]), "offsetDistance" : 25 * mm});
        }
    });
